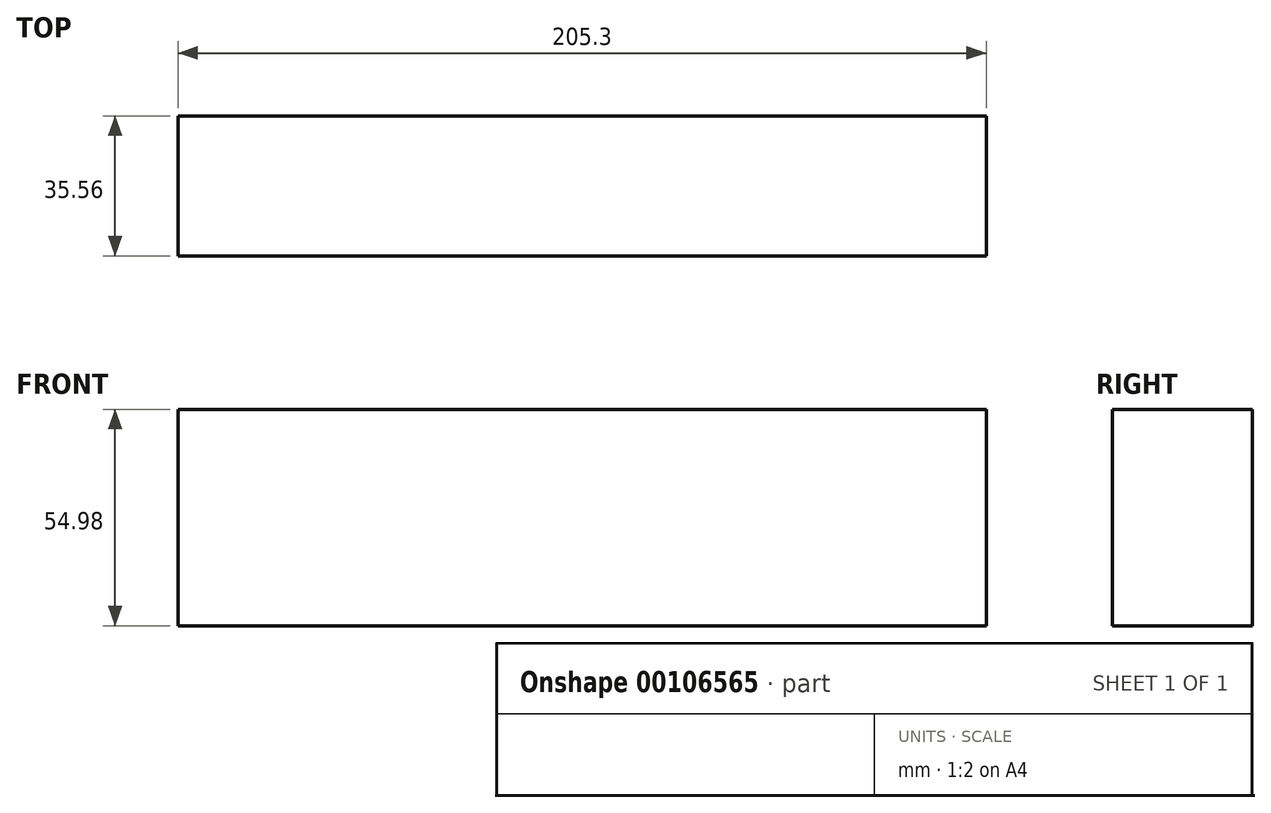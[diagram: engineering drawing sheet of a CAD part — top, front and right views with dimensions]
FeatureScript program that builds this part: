
annotation { "Feature Type Name" : "Feature", "Feature Type Description" : "" }
export const myFeature = defineFeature(function(context is Context, id is Id, definition is map)
    precondition{}
    {
        {
            var Q0;
            Q0=qCreatedBy(makeId("Front.planeOp"),FACE);
            var sketch = newSketch(context, id + "F0", { "sketchPlane" : qUnion([Q0])});
            skLineSegment(sketch, "E0.bottom", {"start": v(102.65, 27.5) * mm, "end": v(-102.65, 27.5) * mm});
            skLineSegment(sketch, "E0.top", {"start": v(102.65, -27.5) * mm, "end": v(-102.65, -27.5) * mm});
            skLineSegment(sketch, "E0.left", {"start": v(102.65, 27.5) * mm, "end": v(102.65, -27.5) * mm});
            skLineSegment(sketch, "E0.right", {"start": v(-102.65, 27.5) * mm, "end": v(-102.65, -27.5) * mm});
            skPoint(sketch, "E0.middle", {"position": v(0, 0) * mm});
            skSolve(sketch);
        }
        {
            var Q0;
            Q0=makeQuery(id+"F0.imprint","IMPRINT",FACE,{"disambiguationData":[TD([[makeQuery(id+"F0.imprint","IMPRINT",EDGE,{"derivedFrom":sQuery(id+"F0.wireOp",EDGE,"E0.bottom")}),1.0]])]});
            extrude(context, id + "F1", {"entities" : qUnion([Q0]), "depth" : 35.56 * mm});
        }
    });
